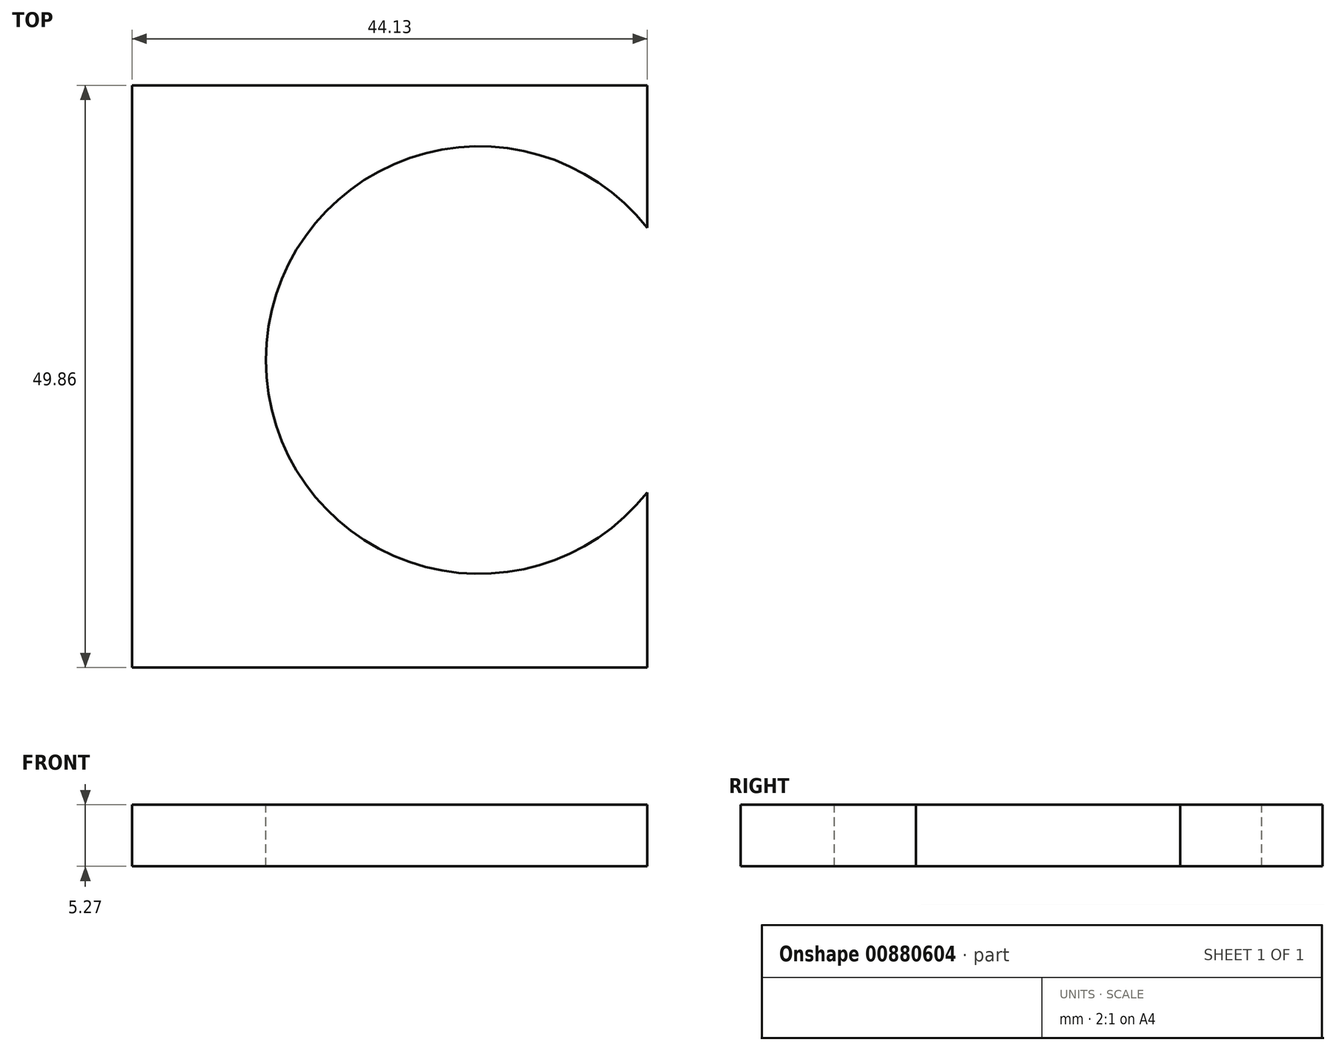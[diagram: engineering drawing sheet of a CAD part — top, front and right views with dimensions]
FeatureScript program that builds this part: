
annotation { "Feature Type Name" : "Feature", "Feature Type Description" : "" }
export const myFeature = defineFeature(function(context is Context, id is Id, definition is map)
    precondition{}
    {
        {
            var Q0;
            Q0=qCreatedBy(makeId("Top.planeOp"),FACE);
            var sketch = newSketch(context, id + "F0", { "sketchPlane" : qUnion([Q0])});
            skLineSegment(sketch, "E0.bottom", {"start": v(0, 0) * mm, "end": v(44.13, 0) * mm});
            skLineSegment(sketch, "E0.top", {"start": v(0, 49.86) * mm, "end": v(44.13, 49.86) * mm});
            skLineSegment(sketch, "E0.left", {"start": v(0, 0) * mm, "end": v(0, 49.86) * mm});
            skLineSegment(sketch, "E0.right", {"start": v(44.13, 0) * mm, "end": v(44.13, 49.86) * mm});
            skSolve(sketch);
        }
        {
            var Q0;
            Q0 = qSketchRegion(id + "F0", true);
            extrude(context, id + "F1", {"entities" : qUnion([Q0]), "depth" : 40.86 * mm, "offsetDistance" : 25.4 * mm});
        }
        {
            var Q0;
            Q0=makeQuery(id+"F1.opExtrude","CAP_FACE",FACE,{"disambiguationData":[OSD([sQuery(id+"F0.wireOp",EDGE,"E0.bottom"),sQuery(id+"F0.wireOp",EDGE,"E0.top"),sQuery(id+"F0.wireOp",EDGE,"E0.left"),sQuery(id+"F0.wireOp",EDGE,"E0.right")])],"isStart":false});
            var sketch = newSketch(context, id + "F2", { "sketchPlane" : qUnion([Q0])});
            skSolve(sketch);
        }
        {
            var Q0;
            Q0=makeQuery(id+"F2.imprint","IMPRINT",FACE,{"disambiguationData":[TD([[makeQuery(id+"F2.imprint","IMPRINT",EDGE,{"derivedFrom":makeQuery(id+"F1.opExtrude","CAP_EDGE",EDGE,{"disambiguationData":[OSD([sQuery(id+"F0.wireOp",EDGE,"E0.bottom")])],"isStart":false})}),1.0]])]});
            extrude(context, id + "F3", {"entities" : qUnion([Q0]), "operationType" : NewBodyOperationType.REMOVE, "oppositeDirection" : true, "depth" : 35.6 * mm, "offsetDistance" : 25.4 * mm});
        }
        {
            var Q0;
            Q0=makeQuery(id+"F3.boolean.opBoolean","COPY",FACE,{"derivedFrom":makeQuery(id+"F3.opExtrude","CAP_FACE",FACE,{"disambiguationData":[OSD([sQuery(id+"F0.wireOp",EDGE,"E0.bottom"),sQuery(id+"F0.wireOp",EDGE,"E0.top"),sQuery(id+"F0.wireOp",EDGE,"E0.left"),sQuery(id+"F0.wireOp",EDGE,"E0.right")])],"isStart":false})});
            var sketch = newSketch(context, id + "F4", { "sketchPlane" : qUnion([Q0])});
            skCircle(sketch, "E1", {"center": v(29.75, 26.34) * mm, "radius": 18.3 * mm});
            skSolve(sketch);
        }
        {
            var Q0;
            Q0 = qSketchRegion(id + "F4", true);
            extrude(context, id + "F5", {"entities" : qUnion([Q0]), "operationType" : NewBodyOperationType.REMOVE, "oppositeDirection" : true, "depth" : 15.32 * mm, "offsetDistance" : 25.4 * mm});
        }
    });
